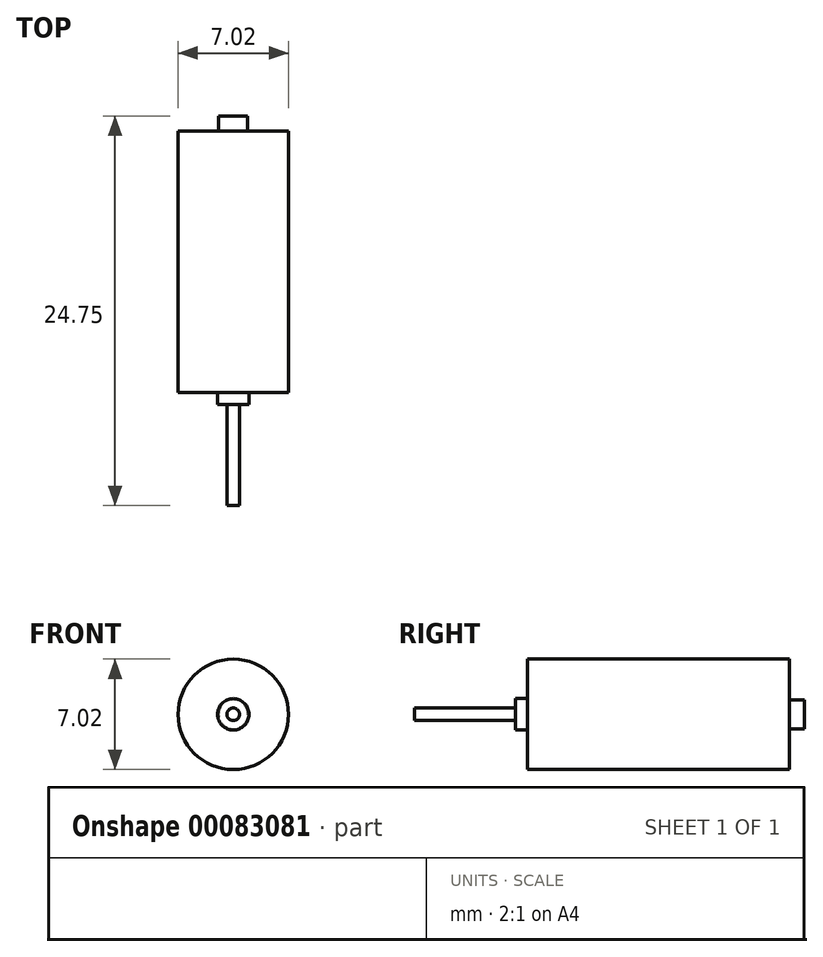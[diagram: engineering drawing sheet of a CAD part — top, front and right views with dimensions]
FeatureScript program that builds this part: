
annotation { "Feature Type Name" : "Feature", "Feature Type Description" : "" }
export const myFeature = defineFeature(function(context is Context, id is Id, definition is map)
    precondition{}
    {
        {
            var Q0;
            Q0=qCreatedBy(makeId("Front.planeOp"),FACE);
            var sketch = newSketch(context, id + "F0", { "sketchPlane" : qUnion([Q0])});
            skCircle(sketch, "E0", {"center": v(0, 0) * mm, "radius": 0.4 * mm});
            skSolve(sketch);
        }
        {
            var Q0;
            Q0=makeQuery(id+"F0.imprint","IMPRINT",FACE,{"disambiguationData":[TD([[makeQuery(id+"F0.imprint","IMPRINT",EDGE,{"derivedFrom":sQuery(id+"F0.wireOp",EDGE,"E0")}),1.0]])]});
            extrude(context, id + "F1", {"entities" : qUnion([Q0]), "oppositeDirection" : true, "depth" : 6.43 * mm});
        }
        {
            var Q0;
            Q0=makeQuery(id+"F1.opExtrude","CAP_FACE",FACE,{"disambiguationData":[OSD([sQuery(id+"F0.wireOp",EDGE,"E0")])],"isStart":false});
            var sketch = newSketch(context, id + "F2", { "sketchPlane" : qUnion([Q0])});
            skCircle(sketch, "E1", {"center": v(0, 0) * mm, "radius": 1 * mm});
            skSolve(sketch);
        }
        {
            var Q0;
            Q0=makeQuery(id+"F2.imprint","IMPRINT",FACE,{"disambiguationData":[TD([[makeQuery(id+"F2.imprint","IMPRINT",EDGE,{"derivedFrom":sQuery(id+"F2.wireOp",EDGE,"E1")}),1.0]])]});
            var Q1;
            Q1=makeQuery(id+"F2.imprint","IMPRINT",FACE,{"disambiguationData":[TD([[makeQuery(id+"F2.imprint","IMPRINT",EDGE,{"derivedFrom":makeQuery(id+"F1.opExtrude","CAP_EDGE",EDGE,{"disambiguationData":[OSD([sQuery(id+"F0.wireOp",EDGE,"E0")])],"isStart":false})}),-1.0]])]});
            extrude(context, id + "F3", {"entities" : qUnion([Q0, Q1]), "operationType" : NewBodyOperationType.ADD, "depth" : 0.75 * mm});
        }
        {
            var Q0;
            Q0=makeQuery(id+"F3.opExtrude","CAP_FACE",FACE,{"disambiguationData":[OSD([sQuery(id+"F2.wireOp",EDGE,"E1")])],"isStart":false});
            var sketch = newSketch(context, id + "F4", { "sketchPlane" : qUnion([Q0])});
            skCircle(sketch, "E2", {"center": v(0, 0) * mm, "radius": 3.5 * mm});
            skSolve(sketch);
        }
        {
            var Q0;
            Q0=makeQuery(id+"F4.imprint","IMPRINT",FACE,{"disambiguationData":[TD([[makeQuery(id+"F4.imprint","IMPRINT",EDGE,{"derivedFrom":sQuery(id+"F4.wireOp",EDGE,"E2")}),1.0]])]});
            var Q1;
            Q1=makeQuery(id+"F4.imprint","IMPRINT",FACE,{"disambiguationData":[TD([[makeQuery(id+"F4.imprint","IMPRINT",EDGE,{"derivedFrom":makeQuery(id+"F3.opExtrude","CAP_EDGE",EDGE,{"disambiguationData":[OSD([sQuery(id+"F2.wireOp",EDGE,"E1")])],"isStart":false})}),1.0]])]});
            extrude(context, id + "F5", {"entities" : qUnion([Q0, Q1]), "operationType" : NewBodyOperationType.ADD, "depth" : 16.62 * mm});
        }
        {
            var Q0;
            Q0=makeQuery(id+"F5.opExtrude","CAP_FACE",FACE,{"disambiguationData":[OSD([sQuery(id+"F4.wireOp",EDGE,"E2")])],"isStart":false});
            var sketch = newSketch(context, id + "F6", { "sketchPlane" : qUnion([Q0])});
            skCircle(sketch, "E3", {"center": v(0, 0) * mm, "radius": 0.92 * mm});
            skSolve(sketch);
        }
        {
            var Q0;
            Q0=makeQuery(id+"F6.imprint","IMPRINT",FACE,{"disambiguationData":[TD([[makeQuery(id+"F6.imprint","IMPRINT",EDGE,{"derivedFrom":sQuery(id+"F6.wireOp",EDGE,"E3")}),1.0]])]});
            extrude(context, id + "F7", {"entities" : qUnion([Q0]), "operationType" : NewBodyOperationType.ADD, "depth" : 0.95 * mm});
        }
    });
